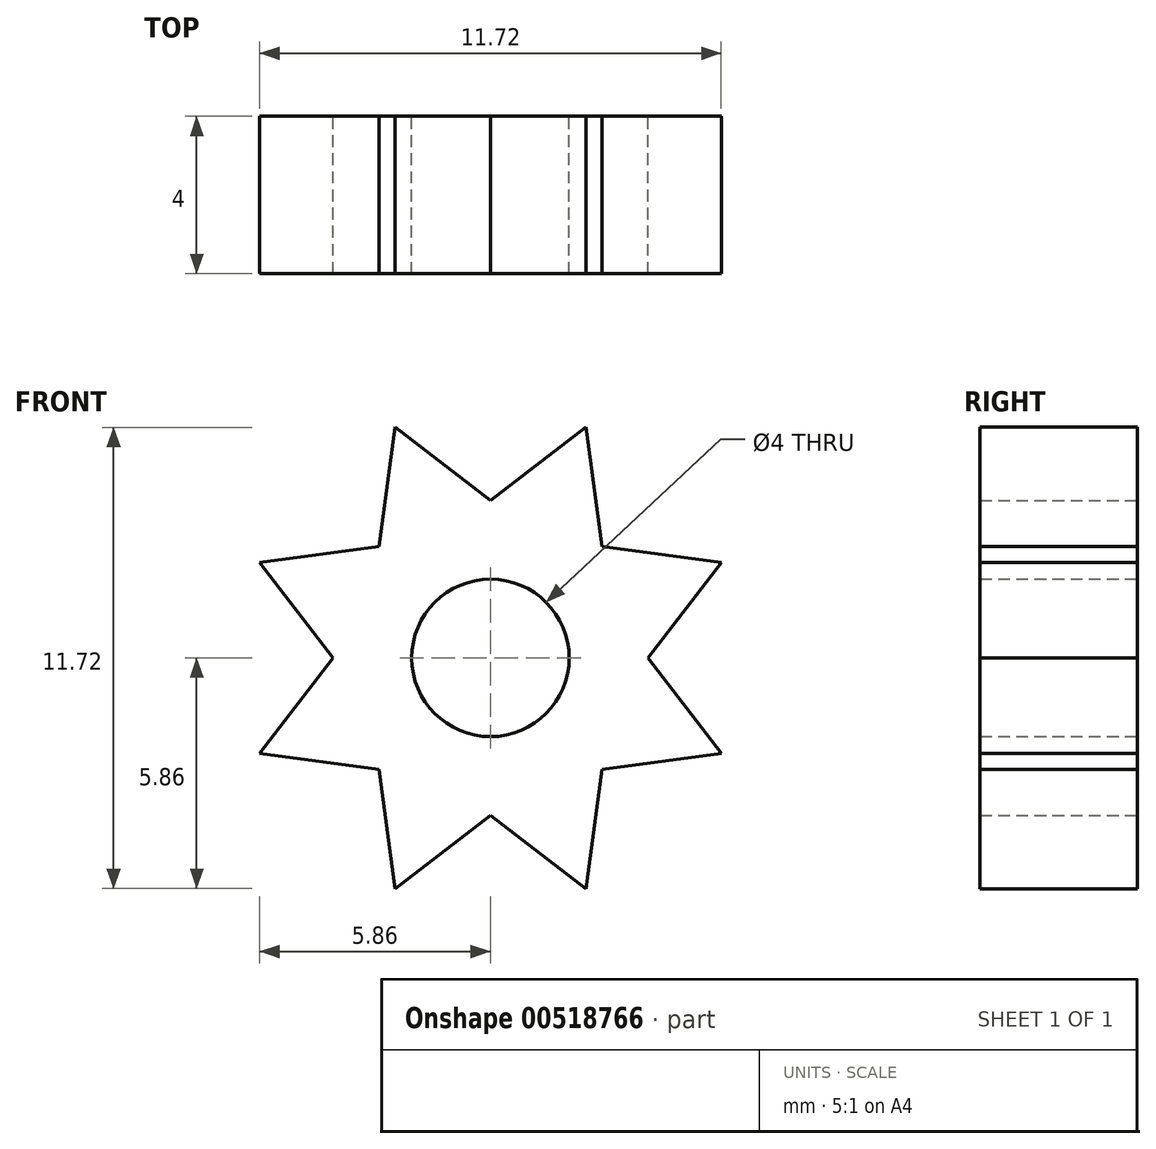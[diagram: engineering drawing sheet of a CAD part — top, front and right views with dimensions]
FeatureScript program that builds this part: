
annotation { "Feature Type Name" : "Feature", "Feature Type Description" : "" }
export const myFeature = defineFeature(function(context is Context, id is Id, definition is map)
    precondition{}
    {
        {
            var Q0;
            Q0=qCreatedBy(makeId("Front.planeOp"),FACE);
            var sketch = newSketch(context, id + "F0", { "sketchPlane" : qUnion([Q0])});
            skCircle(sketch, "E0", {"center": v(0, 0) * mm, "radius": 4 * mm});
            skCircle(sketch, "E1", {"center": v(0, 0) * mm, "radius": 2 * mm});
            skLineSegment(sketch, "E2", {"start": v(0, 0) * mm, "end": v(-2.83, 2.83) * mm, "construction": true});
            skLineSegment(sketch, "E3", {"start": v(-2.83, 2.83) * mm, "end": v(-2.43, 5.86) * mm});
            skLineSegment(sketch, "E4", {"start": v(-2.43, 5.86) * mm, "end": v(0, 4) * mm});
            skLineSegment(sketch, "E5.1.0", {"start": v(-5.86, 2.43) * mm, "end": v(-2.83, 2.83) * mm});
            skLineSegment(sketch, "E5.1.1", {"start": v(-4, 0) * mm, "end": v(-5.86, 2.43) * mm});
            skLineSegment(sketch, "E5.2.0", {"start": v(-5.86, -2.43) * mm, "end": v(-4, 0) * mm});
            skLineSegment(sketch, "E5.2.1", {"start": v(-2.83, -2.83) * mm, "end": v(-5.86, -2.43) * mm});
            skLineSegment(sketch, "E5.3.0", {"start": v(-2.43, -5.86) * mm, "end": v(-2.83, -2.83) * mm});
            skLineSegment(sketch, "E5.3.1", {"start": v(0, -4) * mm, "end": v(-2.43, -5.86) * mm});
            skLineSegment(sketch, "E5.4.0", {"start": v(2.43, -5.86) * mm, "end": v(0, -4) * mm});
            skLineSegment(sketch, "E5.4.1", {"start": v(2.83, -2.83) * mm, "end": v(2.43, -5.86) * mm});
            skLineSegment(sketch, "E5.5.0", {"start": v(5.86, -2.43) * mm, "end": v(2.83, -2.83) * mm});
            skLineSegment(sketch, "E5.5.1", {"start": v(4, 0) * mm, "end": v(5.86, -2.43) * mm});
            skLineSegment(sketch, "E5.6.0", {"start": v(5.86, 2.43) * mm, "end": v(4, 0) * mm});
            skLineSegment(sketch, "E5.6.1", {"start": v(2.83, 2.83) * mm, "end": v(5.86, 2.43) * mm});
            skLineSegment(sketch, "E5.7.0", {"start": v(2.43, 5.86) * mm, "end": v(2.83, 2.83) * mm});
            skLineSegment(sketch, "E5.7.1", {"start": v(0, 4) * mm, "end": v(2.43, 5.86) * mm});
            skSolve(sketch);
        }
        {
            var Q0;
            Q0=qSketchRegion(id+"F0",true);
            extrude(context, id + "F1", {"entities" : qUnion([Q0]), "endBound" : BoundingType.SYMMETRIC, "depth" : 4 * mm, "offsetDistance" : 25 * mm});
        }
    });
